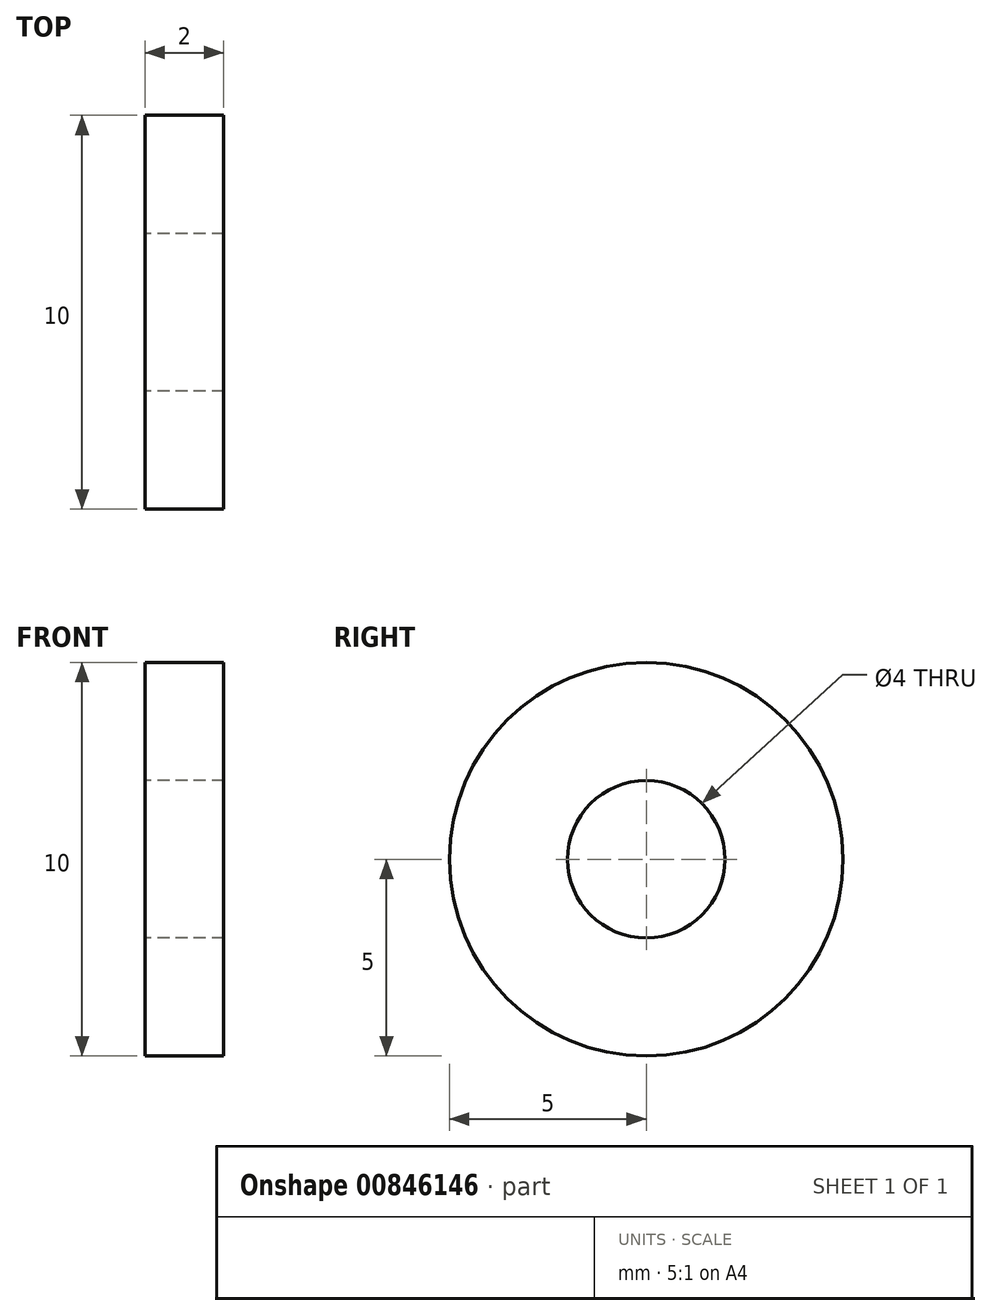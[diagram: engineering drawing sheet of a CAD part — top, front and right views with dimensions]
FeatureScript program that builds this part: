
annotation { "Feature Type Name" : "Feature", "Feature Type Description" : "" }
export const myFeature = defineFeature(function(context is Context, id is Id, definition is map)
    precondition{}
    {
        {
            var Q0;
            Q0=qCreatedBy(makeId("Right.planeOp"),FACE);
            var sketch = newSketch(context, id + "F0", { "sketchPlane" : qUnion([Q0])});
            skCircle(sketch, "E0", {"center": v(0, 0) * mm, "radius": 5 * mm});
            skCircle(sketch, "E1", {"center": v(0, 0) * mm, "radius": 2 * mm});
            skSolve(sketch);
        }
        {
            var Q0;
            Q0 = qSketchRegion(id + "F0", true);
            var Q1;
            Q1=makeQuery(id+"F0.imprint","IMPRINT",FACE,{"disambiguationData":[TD([[makeQuery(id+"F0.imprint","IMPRINT",EDGE,{"derivedFrom":sQuery(id+"F0.wireOp",EDGE,"E0")}),1.0]])]});
            extrude(context, id + "F1", {"entities" : qUnion([Q0, Q1]), "depth" : 2 * mm, "offsetDistance" : 25 * mm});
        }
    });
